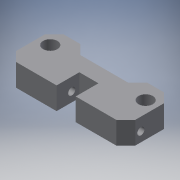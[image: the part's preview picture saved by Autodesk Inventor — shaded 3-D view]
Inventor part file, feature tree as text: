
AUTODESK INVENTOR PART (.ipt)
format: ipt  version: 2016 (Build 200138000, 138)  size: 145,408 bytes
history: native  units: mm
features: extrude x5, sketch x5, chamfer x2
ambient origin geometry x8: Origin, YZ Plane, XZ Plane, XY Plane, X Axis, Y Axis, Z Axis, Center Point
bodies: Solid1 (feature_tree)
feature tree (12):
  extrude  "Extrusion1"  Depth=60.0mm
  extrude  "Extrusion2"  Depth=75.0mm
  extrude  "Extrusion3"  Depth=12.0mm
  extrude  "Extrusion4"  Depth=14.3mm TaperAngle=0.0deg
  extrude  "Extrusion5"  Depth=6.0mm
  chamfer  "Chamfer1"  Distance=4.5mm
  chamfer  "Chamfer2"  Distance=15.0mm
  sketch  "Sketch1"  dims[d0=9.0mm d1=60.0mm]
  sketch  "Sketch2"  dims[d2=40.0mm d3=75.0mm]
  sketch  "Sketch3"  dims[d4=14.0mm d5=0.0mm d6=12.0mm]
  sketch  "Sketch4"  dims[d7=14.3mm d8=15.0mm d9=0.0mm]
  sketch  "Sketch5"  dims[d10=8.0mm d11=9.5mm d12=4.5mm d13=15.0mm d14=0.0mm d15=10.0mm d16=15.0mm d17=0.0mm d18=30.0mm d19=6.0mm d20=10.0mm d21=0.0mm d22=6.0mm d23=2.0mm d24=45.0deg d25=6.0mm d26=2.0mm d27=45.0deg]
